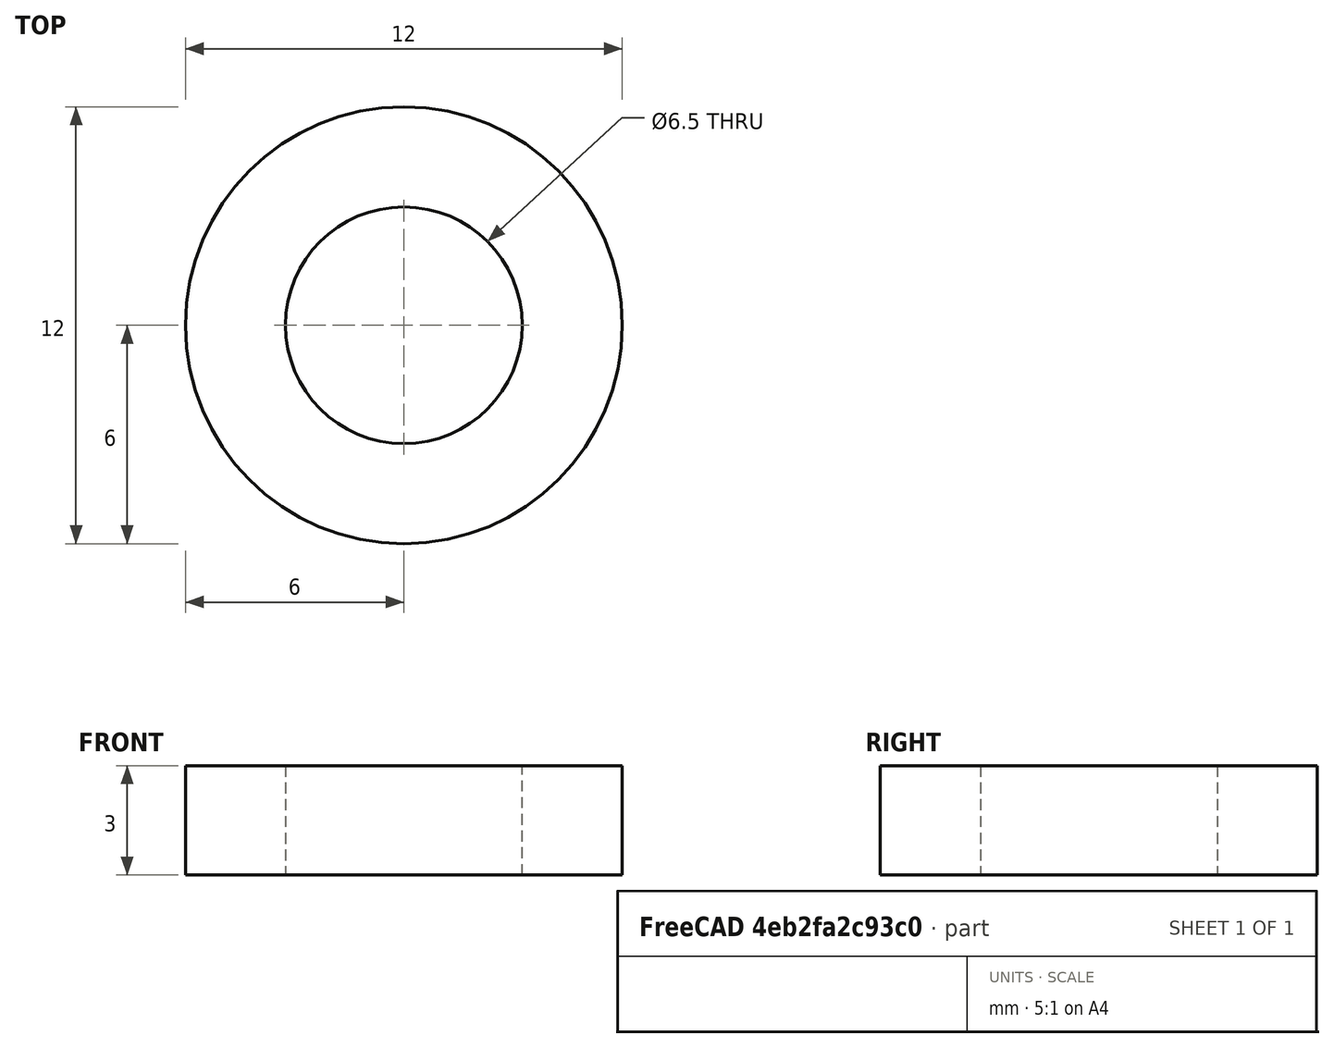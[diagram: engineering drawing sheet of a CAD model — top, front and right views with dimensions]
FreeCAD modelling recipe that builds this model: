
FCSTD DOCUMENT  (FreeCAD 1.0R39109 (Git))
Label: spacer_ring
License: All rights reserved
LicenseURL: http://en.wikipedia.org/wiki/All_rights_reserved
objects: Spreadsheet::Sheet×1, Sketcher::SketchObject×1, PartDesign::Pad×1, PartDesign::Body×1
note: 6 computed .brp shape members not serialized (recipe doc carries the construction recipe); baked Part::Feature solids carry a one-line shape summary decoded from their .brp

FEATURE [Spreadsheet::Sheet] Spreadsheet
  cells = A1='Width; B1='Center hole; C1='Height; A2(ringDia)=12; B2(ringHoleDia)=6.5; C2(ringThick)=3
FEATURE [Sketcher::SketchObject] Sketch
  ArcFitTolerance = 0
  AttachmentSupport = -> [XY_Plane]
  FullyConstrained = true
  MakeInternals = false
  MapMode = 5
  expr: Constraints[2] = Spreadsheet.ringHoleDia
  expr: Constraints[3] = Spreadsheet.ringDia
  sketch-geometry (2):
    g0: Circle CenterX=0 CenterY=0 CenterZ=0 NormalX=0 NormalY=0 NormalZ=1 AngleXU=0 Radius=6
    g1: Circle CenterX=0 CenterY=0 CenterZ=0 NormalX=0 NormalY=0 NormalZ=1 AngleXU=0 Radius=3.25
  constraints (4):
    c: Coincident(g0,g-1)
    c: Coincident(g1,g0)
    c: Diameter(g1) = 6.5
    c: Diameter(g0) = 12
FEATURE [PartDesign::Pad] Pad  label="ring"
  Direction = (0,0,1)
  Length = 3
  Length2 = 10
  Profile = -> Sketch
  ReferenceAxis = -> Sketch [N_Axis]
  Suppressed = false
  Type = 0
  expr: Length = Spreadsheet.ringThick
FEATURE [PartDesign::Body] Body
  AllowCompound = false
  Group = -> [Sketch,Pad]
  Origin = -> Origin
  Tip = -> Pad
